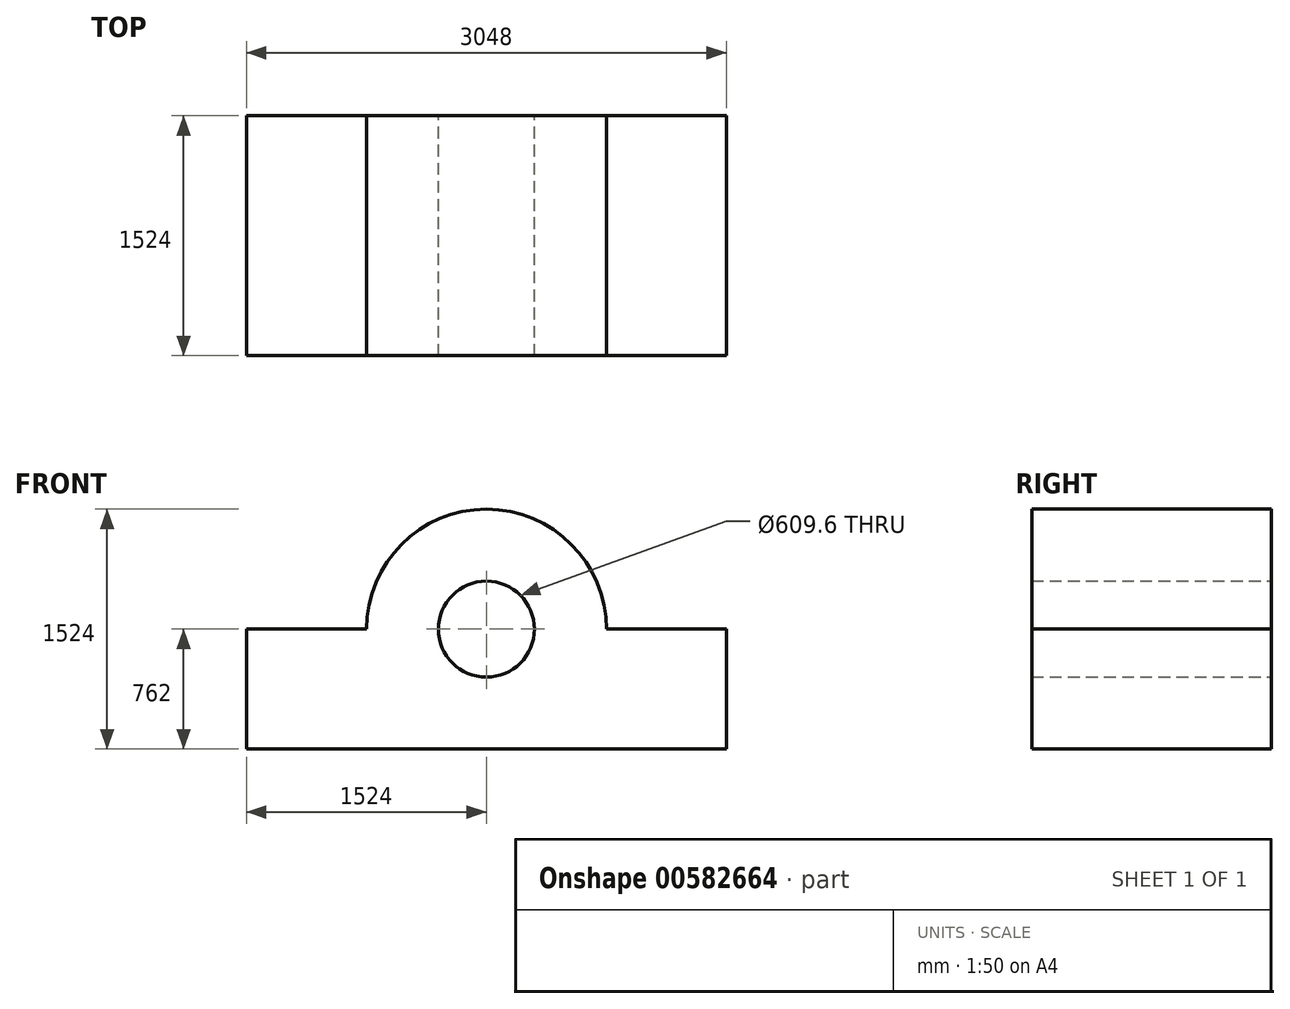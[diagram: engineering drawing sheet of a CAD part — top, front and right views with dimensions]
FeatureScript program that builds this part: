
annotation { "Feature Type Name" : "Feature", "Feature Type Description" : "" }
export const myFeature = defineFeature(function(context is Context, id is Id, definition is map)
    precondition{}
    {
        {
            var Q0;
            Q0=qCreatedBy(makeId("Front.planeOp"),FACE);
            var sketch = newSketch(context, id + "F0", { "sketchPlane" : qUnion([Q0])});
            skLineSegment(sketch, "E0", {"start": v(0, 0) * mm, "end": v(3048, 0) * mm});
            skLineSegment(sketch, "E1", {"start": v(0, 0) * mm, "end": v(0, 762) * mm});
            skLineSegment(sketch, "E2", {"start": v(0, 762) * mm, "end": v(762, 762) * mm});
            skLineSegment(sketch, "E3", {"start": v(3048, 762) * mm, "end": v(3048, 0) * mm});
            skCircle(sketch, "E4", {"center": v(1524, 762) * mm, "radius": 304.8 * mm});
            skArc(sketch, "E5", {"start": v(2286, 762) * mm, "mid": v(1524, 1524) * mm, "end": v(762, 762) * mm});
            skLineSegment(sketch, "E6.trimOffspring", {"start": v(2286, 762) * mm, "end": v(3048, 762) * mm});
            skSolve(sketch);
        }
        {
            var Q0;
            Q0=makeQuery(id+"F0.imprint","IMPRINT",FACE,{"disambiguationData":[TD([[makeQuery(id+"F0.imprint","IMPRINT",EDGE,{"derivedFrom":sQuery(id+"F0.wireOp",EDGE,"E0")}),1.0]])]});
            extrude(context, id + "F1", {"entities" : qUnion([Q0]), "depth" : 1524 * mm, "offsetDistance" : 25.4 * mm});
        }
    });
